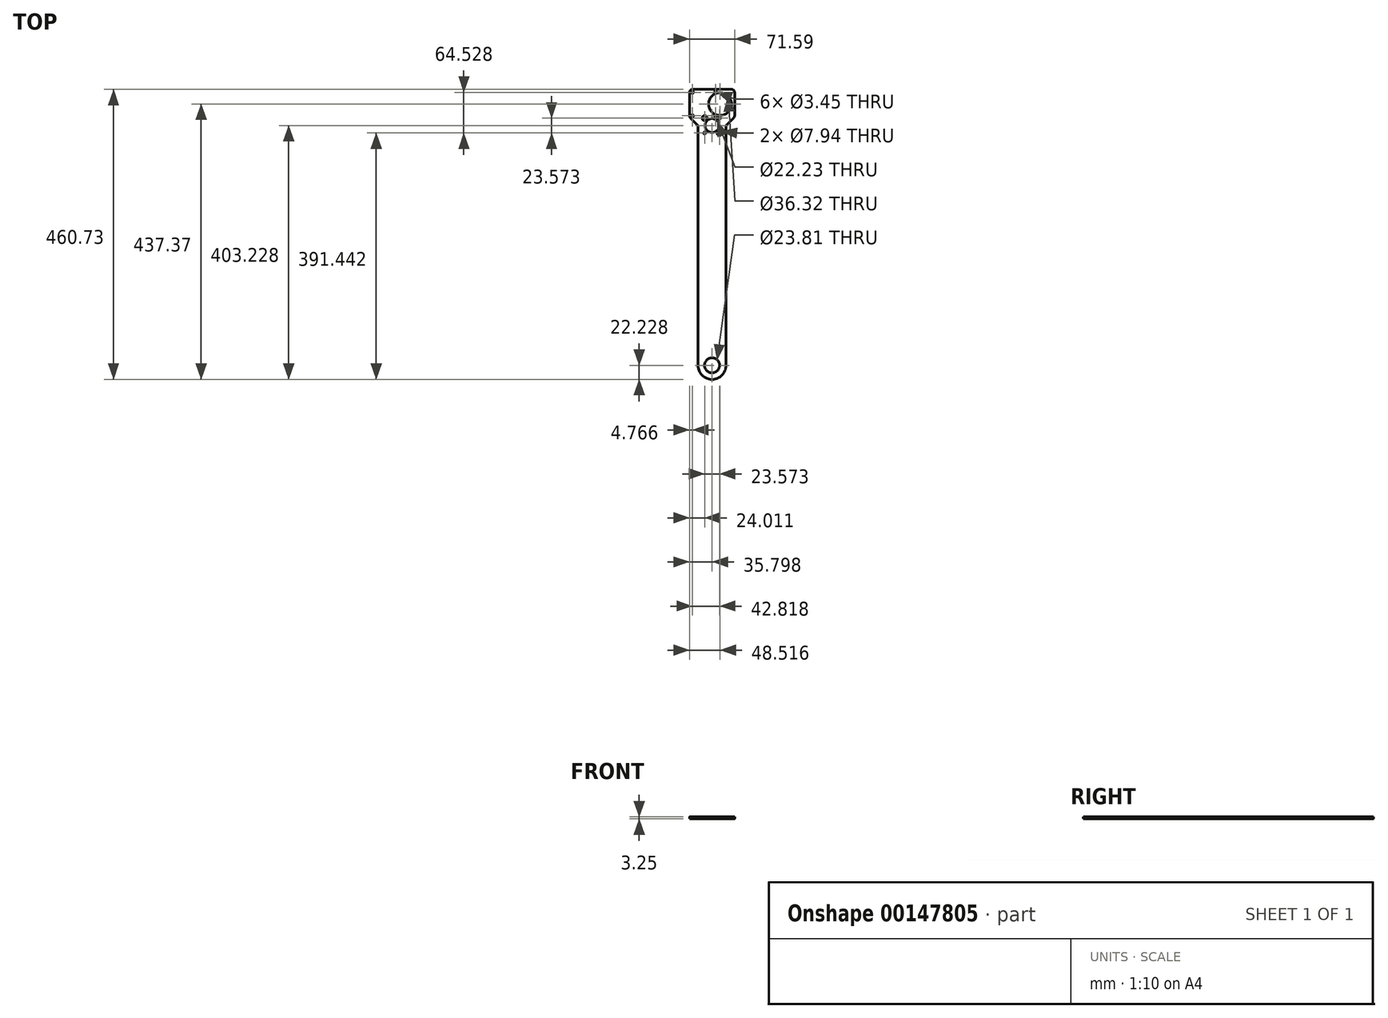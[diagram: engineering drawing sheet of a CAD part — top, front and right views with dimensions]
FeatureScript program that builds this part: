
annotation { "Feature Type Name" : "Feature", "Feature Type Description" : "" }
export const myFeature = defineFeature(function(context is Context, id is Id, definition is map)
    precondition{}
    {
        {
            var Q0;
            Q0=qCreatedBy(makeId("Top.planeOp"),FACE);
            var sketch = newSketch(context, id + "F0", { "sketchPlane" : qUnion([Q0])});
            skLineSegment(sketch, "E0.bottom", {"start": v(18.31, -18.6) * mm, "end": v(-18.31, -18.6) * mm, "construction": true});
            skLineSegment(sketch, "E0.top", {"start": v(18.31, 18.6) * mm, "end": v(-18.31, 18.6) * mm, "construction": true});
            skLineSegment(sketch, "E0.left", {"start": v(18.31, -18.6) * mm, "end": v(18.31, 18.6) * mm, "construction": true});
            skLineSegment(sketch, "E0.right", {"start": v(-18.31, -18.6) * mm, "end": v(-18.31, 18.6) * mm, "construction": true});
            skPoint(sketch, "E0.middle", {"position": v(0, 0) * mm});
            skCircle(sketch, "E1", {"center": v(-18.31, 18.6) * mm, "radius": 1.73 * mm});
            skCircle(sketch, "E2", {"center": v(-18.31, -18.6) * mm, "radius": 1.73 * mm});
            skCircle(sketch, "E3", {"center": v(18.31, -18.6) * mm, "radius": 1.73 * mm});
            skCircle(sketch, "E4", {"center": v(18.31, 18.6) * mm, "radius": 1.73 * mm});
            skLineSegment(sketch, "E5", {"start": v(-18.31, 18.6) * mm, "end": v(-23.08, 18.6) * mm, "construction": true});
            skLineSegment(sketch, "E6", {"start": v(-18.31, 18.6) * mm, "end": v(-18.31, 23.36) * mm, "construction": true});
            skLineSegment(sketch, "E7", {"start": v(0, 0) * mm, "end": v(25.44, 0) * mm, "construction": true});
            skLineSegment(sketch, "E8", {"start": v(-23.08, -18.6) * mm, "end": v(-23.08, 23.36) * mm});
            skLineSegment(sketch, "E9", {"start": v(-23.08, 23.36) * mm, "end": v(48.51, 23.36) * mm});
            skLineSegment(sketch, "E10", {"start": v(48.51, 23.36) * mm, "end": v(48.51, -18.6) * mm});
            skLineSegment(sketch, "E11", {"start": v(12.72, 0) * mm, "end": v(12.72, -34.14) * mm, "construction": true});
            skArc(sketch, "E12", {"start": v(-23.08, -18.6) * mm, "mid": v(-22.71, -20.42) * mm, "end": v(-21.68, -21.97) * mm});
            skLineSegment(sketch, "E13", {"start": v(12.72, 0) * mm, "end": v(12.72, 23.36) * mm, "construction": true});
            skLineSegment(sketch, "E14", {"start": v(-21.68, -21.97) * mm, "end": v(-9.5, -34.14) * mm});
            skArc(sketch, "E15", {"start": v(47.12, -21.97) * mm, "mid": v(48.15, -20.42) * mm, "end": v(48.51, -18.6) * mm});
            skCircle(sketch, "E16", {"center": v(25.44, 0) * mm, "radius": 18.16 * mm});
            skLineSegment(sketch, "E17", {"start": v(47.12, -21.97) * mm, "end": v(34.94, -34.14) * mm});
            skLineSegment(sketch, "E18.bottom", {"start": v(-9.5, -34.14) * mm, "end": v(34.94, -34.14) * mm, "construction": true});
            skLineSegment(sketch, "E18.top", {"start": v(-9.5, -415.14) * mm, "end": v(34.94, -415.14) * mm, "construction": true});
            skLineSegment(sketch, "E18.left", {"start": v(-9.5, -34.14) * mm, "end": v(-9.5, -415.14) * mm});
            skLineSegment(sketch, "E18.right", {"start": v(34.94, -34.14) * mm, "end": v(34.94, -415.14) * mm});
            skCircle(sketch, "E19", {"center": v(12.72, -34.14) * mm, "radius": 22.22 * mm, "construction": true});
            skLineSegment(sketch, "E20.bottom", {"start": v(0.93, -22.36) * mm, "end": v(24.5, -22.36) * mm, "construction": true});
            skLineSegment(sketch, "E20.top", {"start": v(0.93, -45.93) * mm, "end": v(24.5, -45.93) * mm, "construction": true});
            skLineSegment(sketch, "E20.left", {"start": v(0.93, -22.36) * mm, "end": v(0.93, -45.93) * mm, "construction": true});
            skLineSegment(sketch, "E20.right", {"start": v(24.5, -22.36) * mm, "end": v(24.5, -45.93) * mm, "construction": true});
            skCircle(sketch, "E21", {"center": v(0.93, -45.93) * mm, "radius": 5.56 * mm, "construction": true});
            skCircle(sketch, "E22", {"center": v(0.93, -45.93) * mm, "radius": 1.73 * mm});
            skCircle(sketch, "E23", {"center": v(0.93, -22.36) * mm, "radius": 3.97 * mm});
            skCircle(sketch, "E24", {"center": v(24.5, -22.36) * mm, "radius": 1.73 * mm});
            skCircle(sketch, "E25", {"center": v(24.5, -45.93) * mm, "radius": 3.97 * mm});
            skCircle(sketch, "E26", {"center": v(12.72, -34.14) * mm, "radius": 11.11 * mm});
            skArc(sketch, "E27", {"start": v(-9.5, -415.14) * mm, "mid": v(12.72, -437.37) * mm, "end": v(34.94, -415.14) * mm});
            skCircle(sketch, "E28", {"center": v(12.72, -415.14) * mm, "radius": 11.9 * mm});
            skSolve(sketch);
        }
        {
            var Q0;
            Q0=qSketchRegion(id+"F0",true);
            extrude(context, id + "F1", {"entities" : qUnion([Q0]), "depth" : 3.25 * mm});
        }
        {
            var Q0;
            Q0=makeQuery(id+"F1.opExtrude","SWEPT_EDGE",EDGE,{"disambiguationData":[OSD([sQuery(id+"F0.wireOp",EDGE,"E8"),sQuery(id+"F0.wireOp",EDGE,"E9")])]});
            var Q1;
            Q1=makeQuery(id+"F1.opExtrude","SWEPT_EDGE",EDGE,{"disambiguationData":[OSD([sQuery(id+"F0.wireOp",EDGE,"E9"),sQuery(id+"F0.wireOp",EDGE,"E10")])]});
            fillet(context, id + "F2", {"entities" : qUnion([Q0, Q1]), "radius" : 4.76 * mm, "tangentPropagation" : true, "allowEdgeOverflow" : false});
        }
    });
